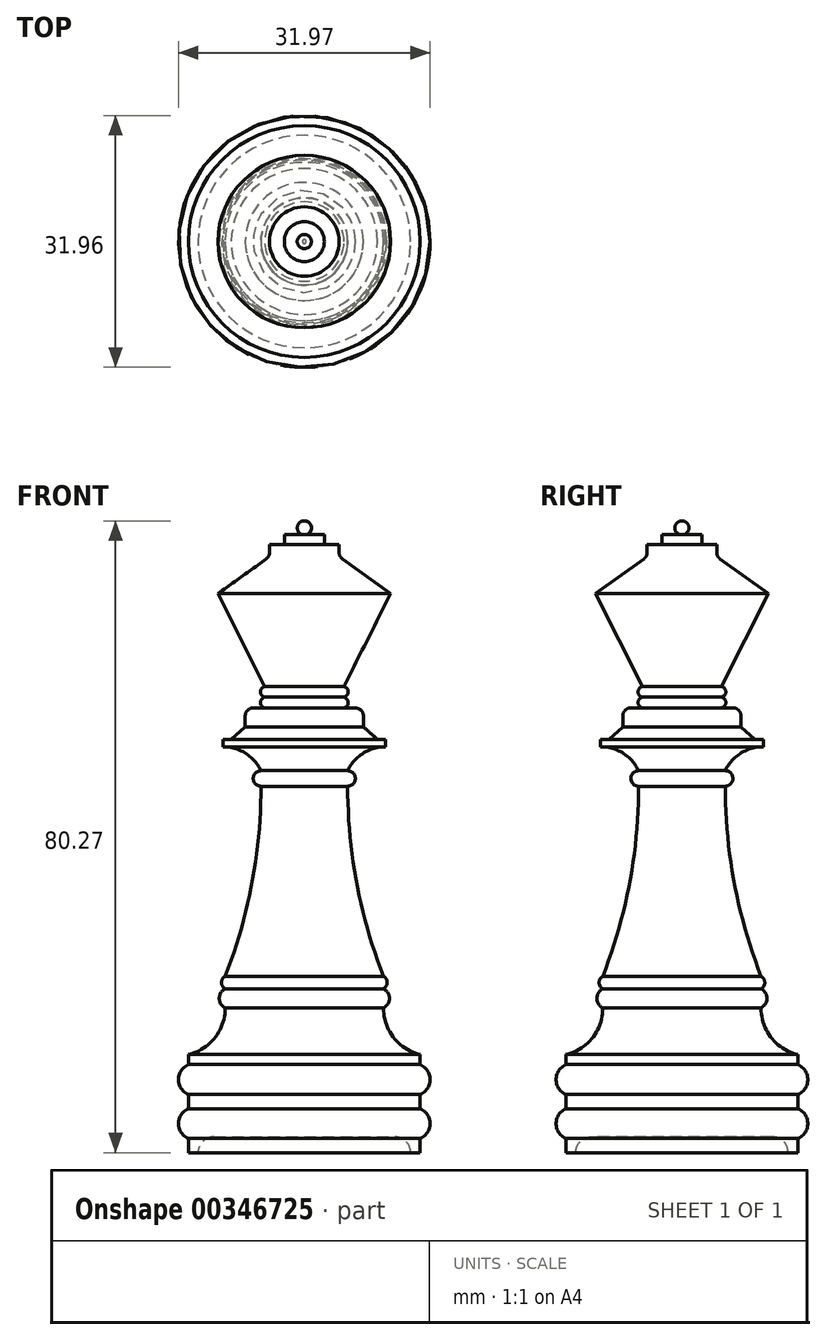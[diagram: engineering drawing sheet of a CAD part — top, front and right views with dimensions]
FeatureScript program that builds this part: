
annotation { "Feature Type Name" : "Feature", "Feature Type Description" : "" }
export const myFeature = defineFeature(function(context is Context, id is Id, definition is map)
    precondition{}
    {
        {
            var Q0;
            Q0=qCreatedBy(makeId("Front.planeOp"),FACE);
            var sketch = newSketch(context, id + "F0", { "sketchPlane" : qUnion([Q0])});
            skLineSegment(sketch, "E0", {"start": v(-203.37, 22.76) * mm, "end": v(-188.64, 22.76) * mm});
            skLineSegment(sketch, "E1", {"start": v(-188.64, 22.76) * mm, "end": v(-188.64, 24.55) * mm});
            skLineSegment(sketch, "E2", {"start": v(-188.64, 28.35) * mm, "end": v(-188.64, 30.15) * mm});
            skLineSegment(sketch, "E3", {"start": v(-188.64, 33.94) * mm, "end": v(-188.64, 35.24) * mm});
            skLineSegment(sketch, "E4", {"start": v(-188.64, 35.24) * mm, "end": v(-193.3, 35.24) * mm});
            skLineSegment(sketch, "E5", {"start": v(-193.3, 35.24) * mm, "end": v(-193.3, 41.17) * mm});
            skArc(sketch, "E6", {"start": v(-193.3, 41.17) * mm, "mid": v(-192.56, 42.37) * mm, "end": v(-193.3, 43.57) * mm});
            skArc(sketch, "E7", {"start": v(-193.3, 43.57) * mm, "mid": v(-192.84, 44.37) * mm, "end": v(-193.3, 45.17) * mm});
            skLineSegment(sketch, "E8", {"start": v(-197.86, 69.31) * mm, "end": v(-197.86, 45.17) * mm});
            skLineSegment(sketch, "E9", {"start": v(-197.86, 45.17) * mm, "end": v(-193.3, 45.17) * mm});
            skArc(sketch, "E10", {"start": v(-197.86, 69.31) * mm, "mid": v(-196.88, 70.3) * mm, "end": v(-197.86, 71.28) * mm});
            skLineSegment(sketch, "E11", {"start": v(-197.86, 71.28) * mm, "end": v(-197.86, 74.33) * mm});
            skLineSegment(sketch, "E12", {"start": v(-197.86, 74.33) * mm, "end": v(-193.04, 74.33) * mm});
            skLineSegment(sketch, "E13", {"start": v(-193.04, 74.33) * mm, "end": v(-193.04, 75.27) * mm});
            skLineSegment(sketch, "E14", {"start": v(-193.04, 75.27) * mm, "end": v(-194.08, 75.27) * mm});
            skLineSegment(sketch, "E15", {"start": v(-194.08, 75.27) * mm, "end": v(-195.87, 76.85) * mm});
            skLineSegment(sketch, "E16", {"start": v(-195.87, 76.85) * mm, "end": v(-195.87, 79.26) * mm});
            skLineSegment(sketch, "E17", {"start": v(-195.87, 79.26) * mm, "end": v(-198.32, 79.26) * mm});
            skArc(sketch, "E18", {"start": v(-198.32, 79.26) * mm, "mid": v(-197.8, 79.94) * mm, "end": v(-198.32, 80.62) * mm});
            skLineSegment(sketch, "E19", {"start": v(-198.32, 81.98) * mm, "end": v(-192.4, 93.8) * mm});
            skLineSegment(sketch, "E20", {"start": v(-192.4, 93.8) * mm, "end": v(-198.95, 98.5) * mm});
            skLineSegment(sketch, "E21", {"start": v(-198.95, 98.5) * mm, "end": v(-198.95, 100.04) * mm});
            skLineSegment(sketch, "E22", {"start": v(-198.95, 100.04) * mm, "end": v(-200.83, 100.04) * mm});
            skLineSegment(sketch, "E23", {"start": v(-200.83, 100.04) * mm, "end": v(-200.83, 101.26) * mm});
            skArc(sketch, "E24", {"start": v(-198.32, 80.62) * mm, "mid": v(-197.8, 81.3) * mm, "end": v(-198.32, 81.98) * mm});
            skLineSegment(sketch, "E25", {"start": v(-200.83, 101.26) * mm, "end": v(-203.12, 101.26) * mm});
            skArc(sketch, "E26", {"start": v(-203.37, 103.03) * mm, "mid": v(-202.47, 102.25) * mm, "end": v(-203.12, 101.26) * mm});
            skLineSegment(sketch, "E27", {"start": v(-203.37, 101.26) * mm, "end": v(-203.37, 22.76) * mm});
            skPoint(sketch, "E28", {"position": v(-203.37, 101.26) * mm});
            skLineSegment(sketch, "E29", {"start": v(-203.37, 103.03) * mm, "end": v(-203.37, 101.26) * mm});
            skLineSegment(sketch, "E30", {"start": v(-188.64, 33.94) * mm, "end": v(-188.64, 30.15) * mm});
            skArc(sketch, "E31", {"start": v(-188.64, 30.15) * mm, "mid": v(-187.38, 32.04) * mm, "end": v(-188.64, 33.94) * mm});
            skArc(sketch, "E32", {"start": v(-188.64, 24.55) * mm, "mid": v(-187.38, 26.45) * mm, "end": v(-188.64, 28.35) * mm});
            skSolve(sketch);
        }
        {
            var Q0;
            Q0=makeQuery(id+"F0.imprint","IMPRINT",FACE,{"disambiguationData":[TD([[makeQuery(id+"F0.imprint","IMPRINT",EDGE,{"derivedFrom":sQuery(id+"F0.wireOp",EDGE,"E0")}),1.0]])]});
            var Q1;
            Q1=makeQuery(id+"F0.imprint","IMPRINT",FACE,{"disambiguationData":[TD([[makeQuery(id+"F0.imprint","IMPRINT",EDGE,{"derivedFrom":sQuery(id+"F0.wireOp",EDGE,"E30")}),1.0]])]});
            var Q2;
            Q2=sQuery(id+"F0.wireOp",EDGE,"E27");
            revolve(context, id + "F1", {"entities" : qUnion([Q0, Q1]), "axis" : qUnion([Q2]), "revolveType" : RevolveType.FULL});
        }
        {
            var Q0;
            Q0=makeQuery(id+"F1.opRevolve","SWEPT_EDGE",EDGE,{"disambiguationData":[OSD([sQuery(id+"F0.wireOp",EDGE,"E4"),sQuery(id+"F0.wireOp",EDGE,"E5")])]});
            var Q1;
            Q1=makeQuery(id+"F3.opFillet","BLEND_FACE",FACE,{"disambiguationData":[OSD([sQuery(id+"F0.wireOp",EDGE,"E8"),sQuery(id+"F0.wireOp",EDGE,"E9")])]});
            fillet(context, id + "F2", {"entities" : qUnion([Q0, Q1]), "radius" : 6 * mm, "tangentPropagation" : true, "allowEdgeOverflow" : false});
        }
        {
            var Q0;
            Q0=makeQuery(id+"F1.opRevolve","SWEPT_EDGE",EDGE,{"disambiguationData":[OSD([sQuery(id+"F0.wireOp",EDGE,"E8"),sQuery(id+"F0.wireOp",EDGE,"E9")])]});
            fillet(context, id + "F3", {"entities" : qUnion([Q0]), "radius" : 66.3 * mm, "tangentPropagation" : true, "allowEdgeOverflow" : false});
        }
        {
            var Q0;
            Q0=makeQuery(id+"F1.opRevolve","SWEPT_EDGE",EDGE,{"disambiguationData":[OSD([sQuery(id+"F0.wireOp",EDGE,"E11"),sQuery(id+"F0.wireOp",EDGE,"E12")])]});
            fillet(context, id + "F4", {"entities" : qUnion([Q0]), "radius" : 5.33 * mm, "tangentPropagation" : true, "allowEdgeOverflow" : false});
        }
        {
            var Q0;
            Q0=makeQuery(id+"F1.opRevolve","SWEPT_EDGE",EDGE,{"disambiguationData":[OSD([sQuery(id+"F0.wireOp",EDGE,"E16"),sQuery(id+"F0.wireOp",EDGE,"E17")])]});
            fillet(context, id + "F5", {"entities" : qUnion([Q0]), "radius" : 1 * mm, "tangentPropagation" : true, "allowEdgeOverflow" : false});
        }
        {
            var Q0;
            Q0=makeQuery(id+"F1.opRevolve","SWEPT_EDGE",EDGE,{"disambiguationData":[OSD([sQuery(id+"F0.wireOp",EDGE,"E20"),sQuery(id+"F0.wireOp",EDGE,"E21")])]});
            fillet(context, id + "F6", {"entities" : qUnion([Q0]), "radius" : 1 * mm, "tangentPropagation" : true, "allowEdgeOverflow" : false});
        }
        {
            var Q0;
            Q0=makeQuery(id+"F1.opRevolve","SWEPT_FACE",FACE,{"disambiguationData":[OSD([sQuery(id+"F0.wireOp",EDGE,"E0")])]});
            var sketch = newSketch(context, id + "F7", { "sketchPlane" : qUnion([Q0])});
            skCircle(sketch, "E33", {"center": v(-203.37, 0) * mm, "radius": 13.5 * mm});
            skSolve(sketch);
        }
        {
            var Q0;
            Q0=makeQuery(id+"F7.imprint","IMPRINT",FACE,{"disambiguationData":[TD([[makeQuery(id+"F7.imprint","IMPRINT",EDGE,{"derivedFrom":sQuery(id+"F7.wireOp",EDGE,"E33")}),1.0]])]});
            extrude(context, id + "F8", {"entities" : qUnion([Q0]), "operationType" : NewBodyOperationType.REMOVE, "oppositeDirection" : true, "depth" : 2 * mm});
        }
        {
            var Q0;
            Q0=makeQuery(id+"F8.boolean.opBoolean","COPY",EDGE,{"derivedFrom":makeQuery(id+"F8.opExtrude","CAP_EDGE",EDGE,{"disambiguationData":[OSD([sQuery(id+"F7.wireOp",EDGE,"E33")])],"isStart":false})});
            fillet(context, id + "F9", {"entities" : qUnion([Q0]), "radius" : 2 * mm, "tangentPropagation" : true, "allowEdgeOverflow" : false});
        }
    });
